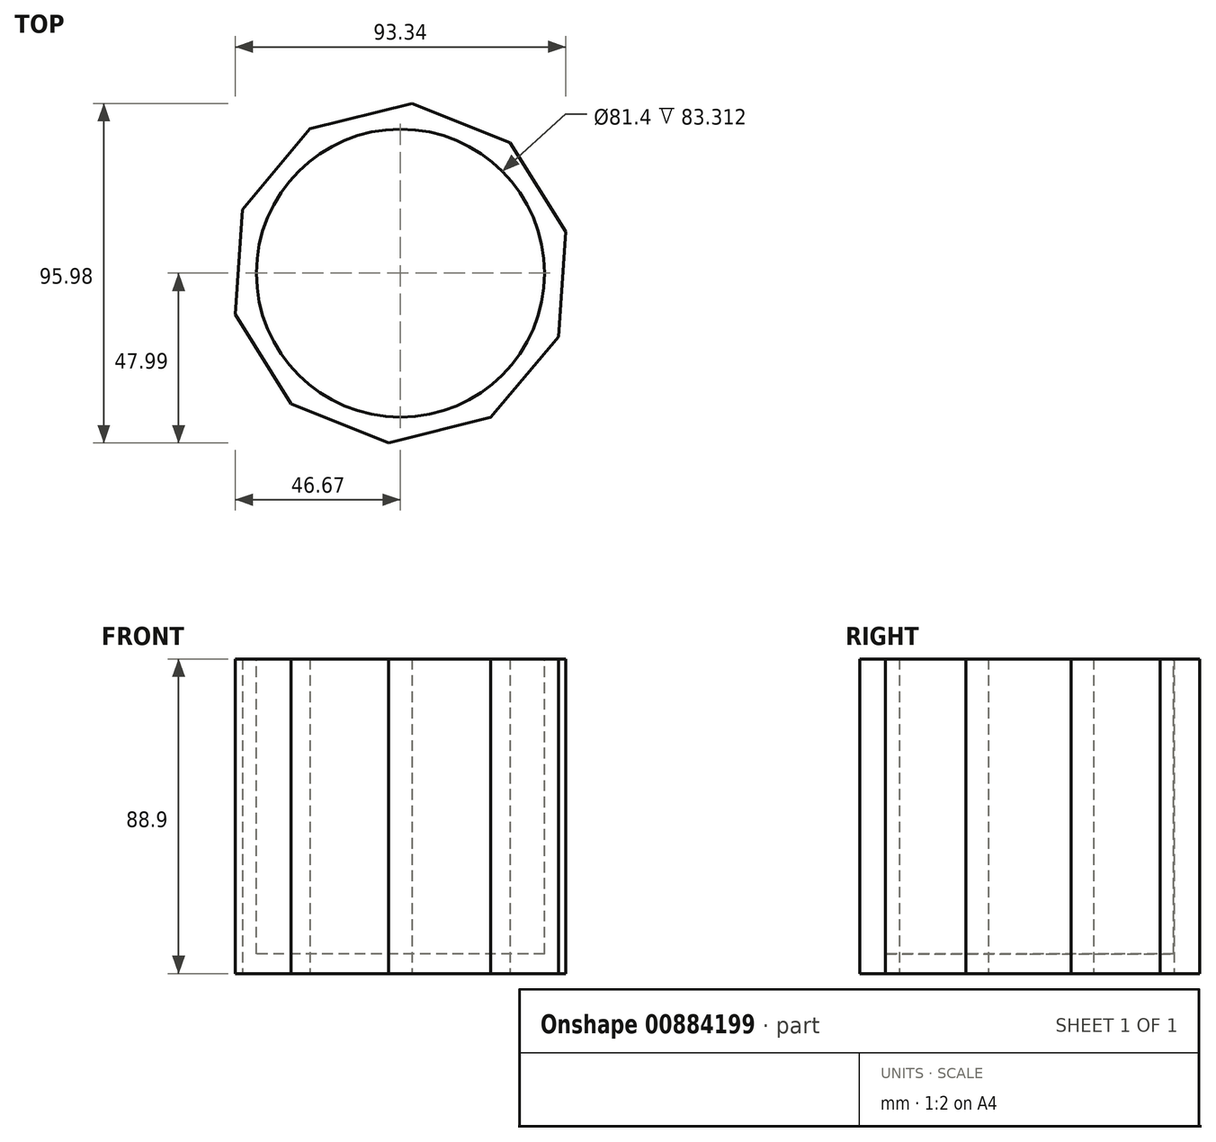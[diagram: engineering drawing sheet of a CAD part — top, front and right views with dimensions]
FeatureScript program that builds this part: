
annotation { "Feature Type Name" : "Feature", "Feature Type Description" : "" }
export const myFeature = defineFeature(function(context is Context, id is Id, definition is map)
    precondition{}
    {
        {
            var Q0;
            Q0=qCreatedBy(makeId("Top.planeOp"),FACE);
            var sketch = newSketch(context, id + "F0", { "sketchPlane" : qUnion([Q0])});
            skCircle(sketch, "E0.cCircle", {"center": v(0, 0) * mm, "radius": 48.1 * mm, "construction": true});
            skLineSegment(sketch, "E0.0", {"start": v(46.67, 11.68) * mm, "end": v(44.62, -17.98) * mm});
            skLineSegment(sketch, "E0.1", {"start": v(44.62, -17.98) * mm, "end": v(25.53, -40.77) * mm});
            skLineSegment(sketch, "E0.2", {"start": v(25.53, -40.77) * mm, "end": v(-3.31, -48) * mm});
            skLineSegment(sketch, "E0.3", {"start": v(-3.31, -48) * mm, "end": v(-30.89, -36.88) * mm});
            skLineSegment(sketch, "E0.4", {"start": v(-30.89, -36.88) * mm, "end": v(-46.67, -11.68) * mm});
            skLineSegment(sketch, "E0.5", {"start": v(-46.67, -11.68) * mm, "end": v(-44.62, 17.98) * mm});
            skLineSegment(sketch, "E0.6", {"start": v(-44.62, 17.98) * mm, "end": v(-25.53, 40.77) * mm});
            skLineSegment(sketch, "E0.7", {"start": v(-25.53, 40.77) * mm, "end": v(3.31, 48) * mm});
            skLineSegment(sketch, "E0.8", {"start": v(3.31, 48) * mm, "end": v(30.89, 36.88) * mm});
            skLineSegment(sketch, "E0.9", {"start": v(30.89, 36.88) * mm, "end": v(46.67, 11.68) * mm});
            skSolve(sketch);
        }
        {
            var Q0;
            Q0=makeQuery(id+"F0.imprint","IMPRINT",FACE,{"disambiguationData":[TD([[makeQuery(id+"F0.imprint","IMPRINT",EDGE,{"derivedFrom":sQuery(id+"F0.wireOp",EDGE,"E0.0")}),-1.0]])]});
            var sketch = newSketch(context, id + "F1", { "sketchPlane" : qUnion([Q0])});
            skSolve(sketch);
        }
        {
            var Q0;
            Q0 = qSketchRegion(id + "F1", true);
            var Q1;
            Q1=makeQuery(id+"F1.imprint","IMPRINT",FACE,{"disambiguationData":[TD([[makeQuery(id+"F1.imprint","IMPRINT",EDGE,{"derivedFrom":makeQuery(id+"F0.imprint","IMPRINT",EDGE,{"derivedFrom":sQuery(id+"F0.wireOp",EDGE,"E0.0")})}),-1.0]])]});
            extrude(context, id + "F2", {"entities" : qUnion([Q0, Q1]), "depth" : 88.9 * mm, "offsetDistance" : 25.4 * mm});
        }
        {
            var Q0;
            Q0=makeQuery(id+"F2.opExtrude","CAP_FACE",FACE,{"disambiguationData":[OSD([sQuery(id+"F0.wireOp",EDGE,"E0.0"),sQuery(id+"F0.wireOp",EDGE,"E0.1"),sQuery(id+"F0.wireOp",EDGE,"E0.2"),sQuery(id+"F0.wireOp",EDGE,"E0.3"),sQuery(id+"F0.wireOp",EDGE,"E0.4"),sQuery(id+"F0.wireOp",EDGE,"E0.5"),sQuery(id+"F0.wireOp",EDGE,"E0.6"),sQuery(id+"F0.wireOp",EDGE,"E0.7"),sQuery(id+"F0.wireOp",EDGE,"E0.8"),sQuery(id+"F0.wireOp",EDGE,"E0.9")])],"isStart":false});
            var sketch = newSketch(context, id + "F3", { "sketchPlane" : qUnion([Q0])});
            skCircle(sketch, "E1", {"center": v(0, 0) * mm, "radius": 40.7 * mm});
            skSolve(sketch);
        }
        {
            var Q0;
            Q0=makeQuery(id+"F3.imprint","IMPRINT",FACE,{"disambiguationData":[TD([[makeQuery(id+"F3.imprint","IMPRINT",EDGE,{"derivedFrom":sQuery(id+"F3.wireOp",EDGE,"E1")}),1.0]])]});
            extrude(context, id + "F4", {"entities" : qUnion([Q0]), "operationType" : NewBodyOperationType.REMOVE, "oppositeDirection" : true, "depth" : 83.31 * mm, "offsetDistance" : 25.4 * mm});
        }
    });
